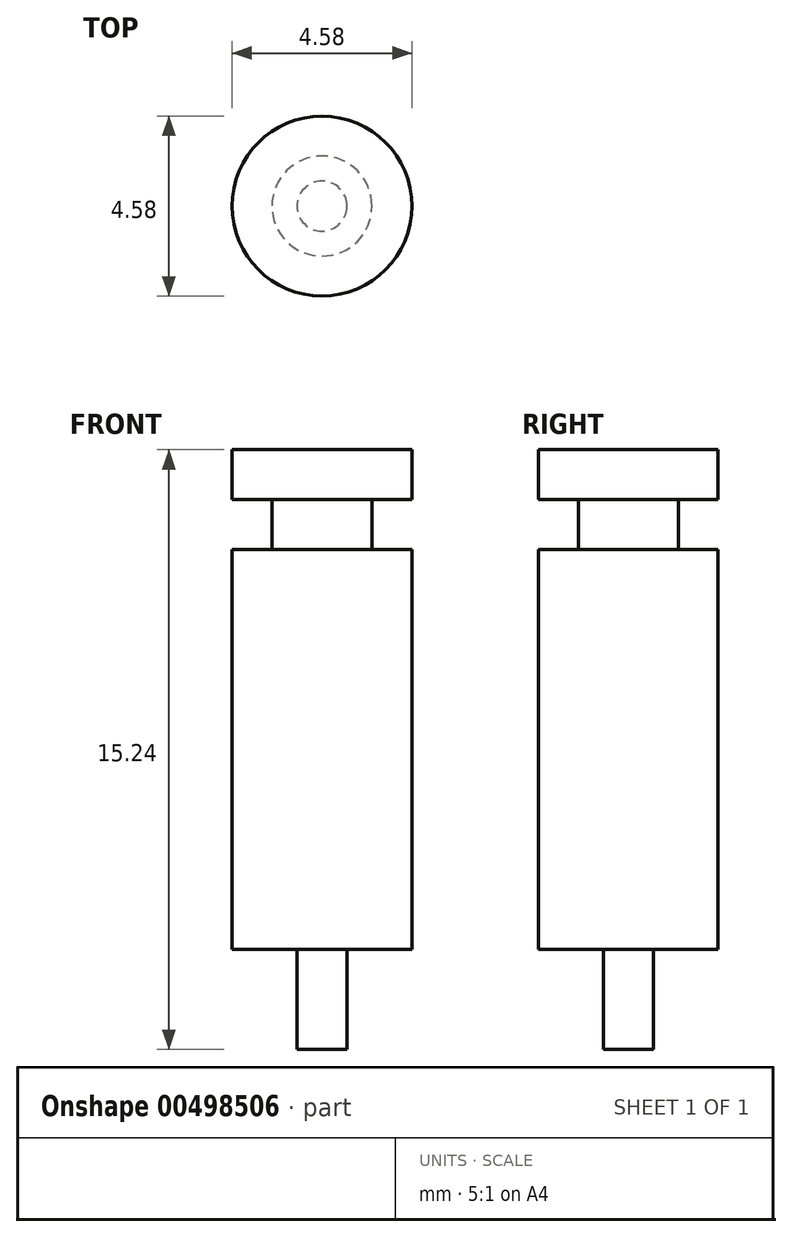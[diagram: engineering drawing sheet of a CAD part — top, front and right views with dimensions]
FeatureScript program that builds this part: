
annotation { "Feature Type Name" : "Feature", "Feature Type Description" : "" }
export const myFeature = defineFeature(function(context is Context, id is Id, definition is map)
    precondition{}
    {
        {
            var Q0;
            Q0=qCreatedBy(makeId("Top.planeOp"),FACE);
            var sketch = newSketch(context, id + "F0", { "sketchPlane" : qUnion([Q0])});
            skCircle(sketch, "E0", {"center": v(0, 0) * mm, "radius": 2.29 * mm});
            skSolve(sketch);
        }
        {
            var Q0;
            Q0 = qSketchRegion(id + "F0", true);
            extrude(context, id + "F1", {"entities" : qUnion([Q0]), "depth" : 10.16 * mm});
        }
        {
            var Q0;
            Q0=makeQuery(id+"F1.opExtrude","CAP_FACE",FACE,{"disambiguationData":[OSD([sQuery(id+"F0.wireOp",EDGE,"E0")])],"isStart":false});
            var sketch = newSketch(context, id + "F2", { "sketchPlane" : qUnion([Q0])});
            skCircle(sketch, "E1", {"center": v(0, 0) * mm, "radius": 1.27 * mm});
            skSolve(sketch);
        }
        {
            var Q0;
            Q0 = qSketchRegion(id + "F2", true);
            extrude(context, id + "F3", {"entities" : qUnion([Q0]), "operationType" : NewBodyOperationType.ADD, "depth" : 1.27 * mm});
        }
        {
            var Q0;
            Q0=makeQuery(id+"F3.opExtrude","CAP_FACE",FACE,{"disambiguationData":[OSD([sQuery(id+"F2.wireOp",EDGE,"E1")])],"isStart":false});
            var sketch = newSketch(context, id + "F4", { "sketchPlane" : qUnion([Q0])});
            skCircle(sketch, "E2", {"center": v(0, 0) * mm, "radius": 2.29 * mm});
            skSolve(sketch);
        }
        {
            var Q0;
            Q0 = qSketchRegion(id + "F4", true);
            extrude(context, id + "F5", {"entities" : qUnion([Q0]), "operationType" : NewBodyOperationType.ADD, "depth" : 1.27 * mm});
        }
        {
            var Q0;
            Q0=makeQuery(id+"F1.opExtrude","CAP_FACE",FACE,{"disambiguationData":[OSD([sQuery(id+"F0.wireOp",EDGE,"E0")])],"isStart":true});
            var sketch = newSketch(context, id + "F6", { "sketchPlane" : qUnion([Q0])});
            skCircle(sketch, "E3", {"center": v(0, 0) * mm, "radius": 0.64 * mm});
            skSolve(sketch);
        }
        {
            var Q0;
            Q0 = qSketchRegion(id + "F6", true);
            extrude(context, id + "F7", {"entities" : qUnion([Q0]), "operationType" : NewBodyOperationType.ADD, "depth" : 2.54 * mm});
        }
    });
